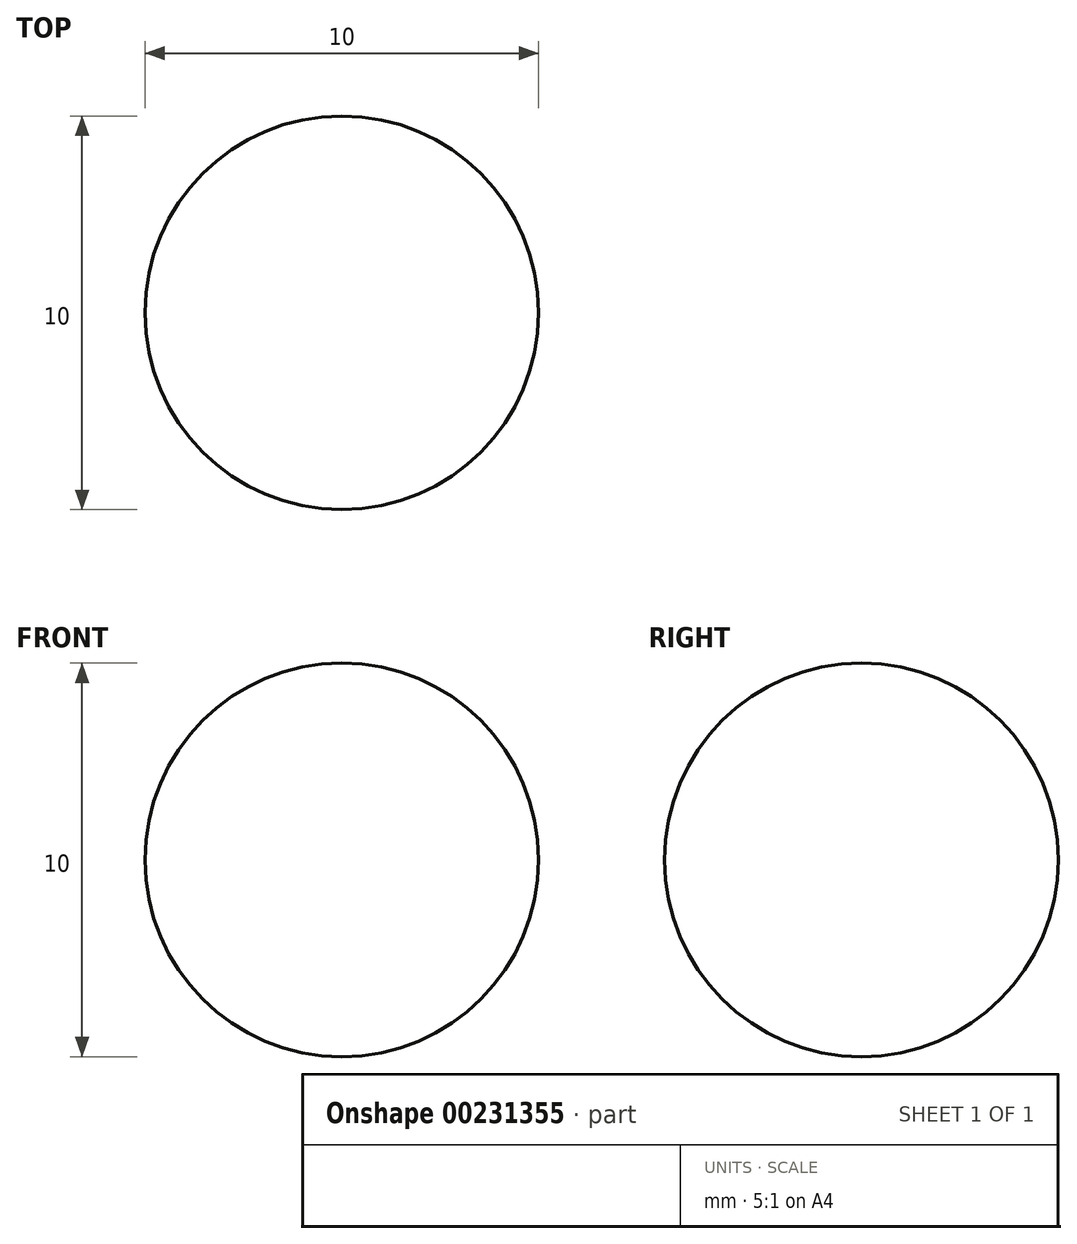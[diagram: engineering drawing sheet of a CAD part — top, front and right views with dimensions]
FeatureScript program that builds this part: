
annotation { "Feature Type Name" : "Feature", "Feature Type Description" : "" }
export const myFeature = defineFeature(function(context is Context, id is Id, definition is map)
    precondition{}
    {
        {
            var Q0;
            Q0=qCreatedBy(makeId("Top.planeOp"),FACE);
            var sketch = newSketch(context, id + "F0", { "sketchPlane" : qUnion([Q0])});
            skCircle(sketch, "E0", {"center": v(0, 0) * mm, "radius": 5 * mm});
            skLineSegment(sketch, "E1", {"start": v(0, 5) * mm, "end": v(0, -5) * mm});
            skSolve(sketch);
        }
        {
            var Q0;
            {var subQ0=sQuery(id+"F0.wireOp",EDGE,"E1");Q0=makeQuery(id+"F0.imprint","IMPRINT",FACE,{"disambiguationData":[TD([[makeQuery(id+"F0.imprint","IMPRINT",EDGE,{"derivedFrom":subQ0}),1.0]])]});}
            var Q1;
            Q1=sQuery(id+"F0.wireOp",EDGE,"E1");
            revolve(context, id + "F1", {"entities" : qUnion([Q0]), "axis" : qUnion([Q1]), "revolveType" : RevolveType.FULL});
        }
    });
